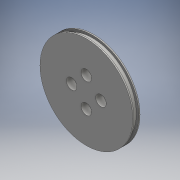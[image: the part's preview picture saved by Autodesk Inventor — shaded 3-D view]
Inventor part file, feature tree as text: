
AUTODESK INVENTOR PART (.ipt)
format: ipt  version: 2016 (Build 200138000, 138)  size: 127,488 bytes
history: native  units: mm
features: sketch x4, extrude x3, hole x1
ambient origin geometry x8: Origin, YZ Plane, XZ Plane, XY Plane, X Axis, Y Axis, Z Axis, Center Point
bodies: Solid1 (feature_tree)
feature tree (8):
  extrude  "Extrusion1"  Depth=0.5mm TaperAngle=0.0deg
  extrude  "Extrusion2"  Depth=2.0mm TaperAngle=0.0deg
  extrude  "Extrusion3"  Depth=0.5mm
  hole  "Hole1"  [1 undecoded]
  sketch  "Sketch1"  dims[d0=38.0mm d1=0.5mm d2=0.0mm]
  sketch  "Sketch2"  dims[d3=36.0mm d4=2.0mm d5=0.0mm]
  sketch  "Sketch3"  dims[d6=0.5mm d7=0.0mm d8=4.35mm]
  sketch  "Sketch4"  dims[d9=6.0mm d10=4.35mm d11=6.0mm d12=4.35mm d13=6.0mm d14=4.35mm d15=6.0mm d16=4.35mm d17=6.0mm d18=4.0mm d19=2.0mm d20=90.0deg d21=8.0mm d22=20.594885mm d23=38.0mm]
note: 1 required parameter value undecoded (feature->parameter linkage not recoverable at this tier; creation-order binding heuristic only, values carry confidence <= 0.55)
